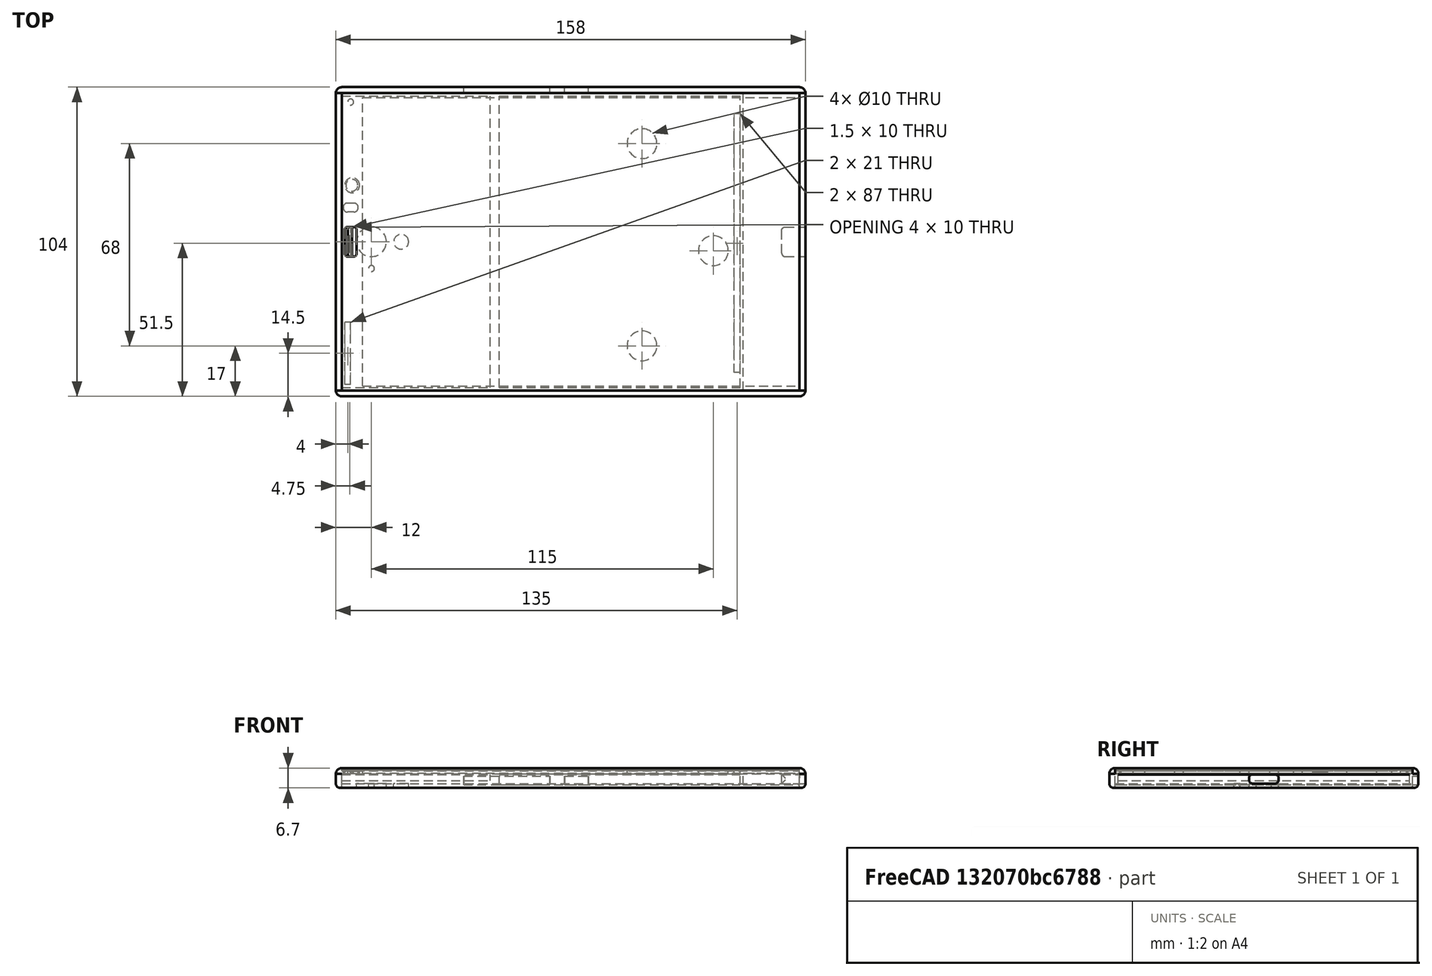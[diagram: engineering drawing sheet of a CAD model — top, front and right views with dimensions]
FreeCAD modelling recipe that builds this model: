
FCSTD DOCUMENT  (FreeCAD 0.15R4671 (Git))
Label: uCromy28_07_2016
License: All rights reserved
LicenseURL: http://en.wikipedia.org/wiki/All_rights_reserved
objects: Part::Cut×19, Part::Box×16, Part::Cylinder×9, Part::Fillet×4, Part::Thickness×1
note: 49 computed .brp shape members not serialized (recipe doc carries the construction recipe); baked Part::Feature solids carry a one-line shape summary decoded from their .brp

FEATURE [Part::Box] Box  label="Cubo"
  Height = 4.7
  Length = 154
  Width = 100
FEATURE [Part::Thickness] Thickness
  Faces = -> Box [Face5]
  Intersection = false
  Join = 0
  Mode = 0
  SelfIntersection = false
  Value = 2
FEATURE [Part::Box] Box001  label="Cubo001"
  Height = 10
  Length = 154
  Placement = pos=(0,0,5.8) rot=(0,0,1;0rad)
  Width = 100
FEATURE [Part::Cut] Cut
  Base = -> Thickness
  Tool = -> Box001
FEATURE [Part::Cylinder] Cylinder  label="Cilindro"
  Angle = 360
  Height = 10
  Placement = pos=(125,47,0) rot=(0,0,1;0rad)
  Radius = 5
FEATURE [Part::Cut] Cut001
  Base = -> Cut
  Tool = -> Cylinder
FEATURE [Part::Cylinder] Cylinder001  label="Cilindro001"
  Angle = 360
  Height = 10
  Placement = pos=(101,83,0) rot=(0,0,1;0rad)
  Radius = 5
FEATURE [Part::Cut] Cut002
  Base = -> Cut001
  Tool = -> Cylinder001
FEATURE [Part::Cylinder] Cylinder002  label="Cilindro002"
  Angle = 360
  Height = 10
  Placement = pos=(101,15,0) rot=(0,0,1;0rad)
  Radius = 5
FEATURE [Part::Cut] Cut003
  Base = -> Cut002
  Tool = -> Cylinder002
FEATURE [Part::Box] Box002  label="Cubo002"
  Height = 10
  Length = 2
  Placement = pos=(1,2,0) rot=(0,0,1;0rad)
  Width = 21
FEATURE [Part::Cut] Cut004
  Base = -> Cut003
  Tool = -> Box002
FEATURE [Part::Box] Box003  label="Cubo003"
  Height = 14
  Length = 1.5
  Placement = pos=(2,45,0) rot=(0,0,1;0rad)
  Width = 10
FEATURE [Part::Cut] Cut005
  Base = -> Cut004
  Tool = -> Box003
FEATURE [Part::Cylinder] Cylinder003  label="Cilindro003"
  Angle = 360
  Height = 10
  Placement = pos=(3,97,0) rot=(0,0,1;0rad)
  Radius = 1
FEATURE [Part::Cut] Cut006
  Base = -> Cut005
  Tool = -> Cylinder003
FEATURE [Part::Cylinder] Cylinder004  label="Cilindro004"
  Angle = 360
  Height = 10
  Placement = pos=(3.4,69,0) rot=(0,0,1;0rad)
  Radius = 2
FEATURE [Part::Cut] Cut007
  Base = -> Cut006
  Tool = -> Cylinder004
FEATURE [Part::Cylinder] Cylinder005  label="Cilindro005"
  Angle = 360
  Height = 10
  Placement = pos=(3.5,69,-4.5) rot=(0,0,1;0rad)
  Radius = 2.5
FEATURE [Part::Cut] Cut008
  Base = -> Cut007
  Tool = -> Cylinder005
FEATURE [Part::Box] Box004  label="Cubo004"
  Height = 10
  Length = 5
  Placement = pos=(0.5,58,0) rot=(0,0,1;0rad)
  Width = 3
FEATURE [Part::Fillet] Fillet
  Base = -> Box004
  Edges = 4 edges r=1.4: [Edge1,Edge3,Edge5,Edge7]
  Placement = pos=(0,2,0) rot=(0,0,1;0rad)
FEATURE [Part::Cut] Cut009
  Base = -> Cut008
  Tool = -> Fillet
FEATURE [Part::Box] Box005  label="Pantalla"
  Height = 1
  Length = 147
  Placement = pos=(7,1.5,5) rot=(0,0,1;0rad)
  Width = 97
FEATURE [Part::Box] Box006  label="Cubo006"
  Height = 0.5
  Length = 154
  Placement = pos=(0,0,6) rot=(0,0,1;0rad)
  Width = 100
FEATURE [Part::Box] Box007  label="Cubo007"
  Height = 10
  Length = 4
  Placement = pos=(1,45,6) rot=(0,0,1;0rad)
  Width = 10
FEATURE [Part::Fillet] Fillet001
  Base = -> Box007
  Edges = 4 edges r=1: [Edge1,Edge3,Edge5,Edge7]
FEATURE [Part::Box] Box008  label="trasera"
  Height = 1.5
  Length = 154
  Width = 100
FEATURE [Part::Fillet] Fillet002  label="Chasis"
  Base = -> Cut009
  Edges = 4 edges r=1.5: [Edge34,Edge36,Edge38,Edge40]
FEATURE [Part::Cylinder] Cylinder006  label="Cilindro006"
  Angle = 360
  Height = 10
  Placement = pos=(10,50,-7) rot=(0,0,1;0rad)
  Radius = 5
FEATURE [Part::Cylinder] Cylinder007  label="Cilindro007"
  Angle = 360
  Height = 10
  Placement = pos=(20,50,-7) rot=(0,0,1;0rad)
  Radius = 2.5
FEATURE [Part::Cut] Cut014
  Base = -> Box008
  Tool = -> Cylinder007
FEATURE [Part::Cut] Cut015
  Base = -> Cut014
  Tool = -> Cylinder006
FEATURE [Part::Cylinder] Cylinder008  label="Cilindro008"
  Angle = 360
  Height = 10
  Placement = pos=(10,41,0) rot=(0,0,1;0rad)
  Radius = 1
FEATURE [Part::Cut] Cut016  label="trasera001"
  Base = -> Cut015
  Tool = -> Cylinder008
FEATURE [Part::Box] Box009  label="Cubo008"
  Height = 3
  Length = 8
  Placement = pos=(75,100,1) rot=(0,0,1;0rad)
  Width = 5
FEATURE [Part::Box] Box010  label="Cubo009"
  Height = 3
  Length = 29
  Placement = pos=(41,100,1) rot=(0,0,1;0rad)
  Width = 5
FEATURE [Part::Cut] Cut017
  Base = -> Fillet002
  Tool = -> Box009
FEATURE [Part::Cut] Cut018
  Base = -> Cut017
  Tool = -> Box010
FEATURE [Part::Cut] Cut019  label="Touch"
  Base = -> Box006
  Tool = -> Fillet001
FEATURE [Part::Box] Box011  label="Electronics"
  Height = 2
  Length = 50
  Placement = pos=(0,1,2.5) rot=(0,0,1;0rad)
  Width = 98
FEATURE [Part::Box] Box012  label="Battery"
  Height = 3.5
  Length = 81
  Placement = pos=(53,1,1) rot=(0,0,1;0rad)
  Width = 98
FEATURE [Part::Box] Box013  label="SoundBuffer"
  Height = 4
  Length = 19
  Placement = pos=(135,0,1) rot=(0,0,1;0rad)
  Width = 100
FEATURE [Part::Box] Box014  label="Cubo010"
  Height = 10
  Length = 2
  Placement = pos=(132,6,1) rot=(0,0,1;0rad)
  Width = 87
FEATURE [Part::Cut] Cut020  label="Chassis"
  Base = -> Cut018
  Tool = -> Box014
FEATURE [Part::Box] Box015  label="Cubo011"
  Height = 3
  Length = 11
  Placement = pos=(148,45,1.5) rot=(0,0,1;0rad)
  Width = 10
FEATURE [Part::Fillet] Fillet003
  Base = -> Box015
  Edges = 8 edges r=1.2: [Edge1,Edge3,Edge5,Edge7,Edge9,Edge10,Edge11,Edge12]
FEATURE [Part::Cut] Cut021
  Base = -> Cut020
  Tool = -> Fillet003
FEATURE [Part::Cut] Cut022
  Base = -> Box013
  Tool = -> Fillet003
